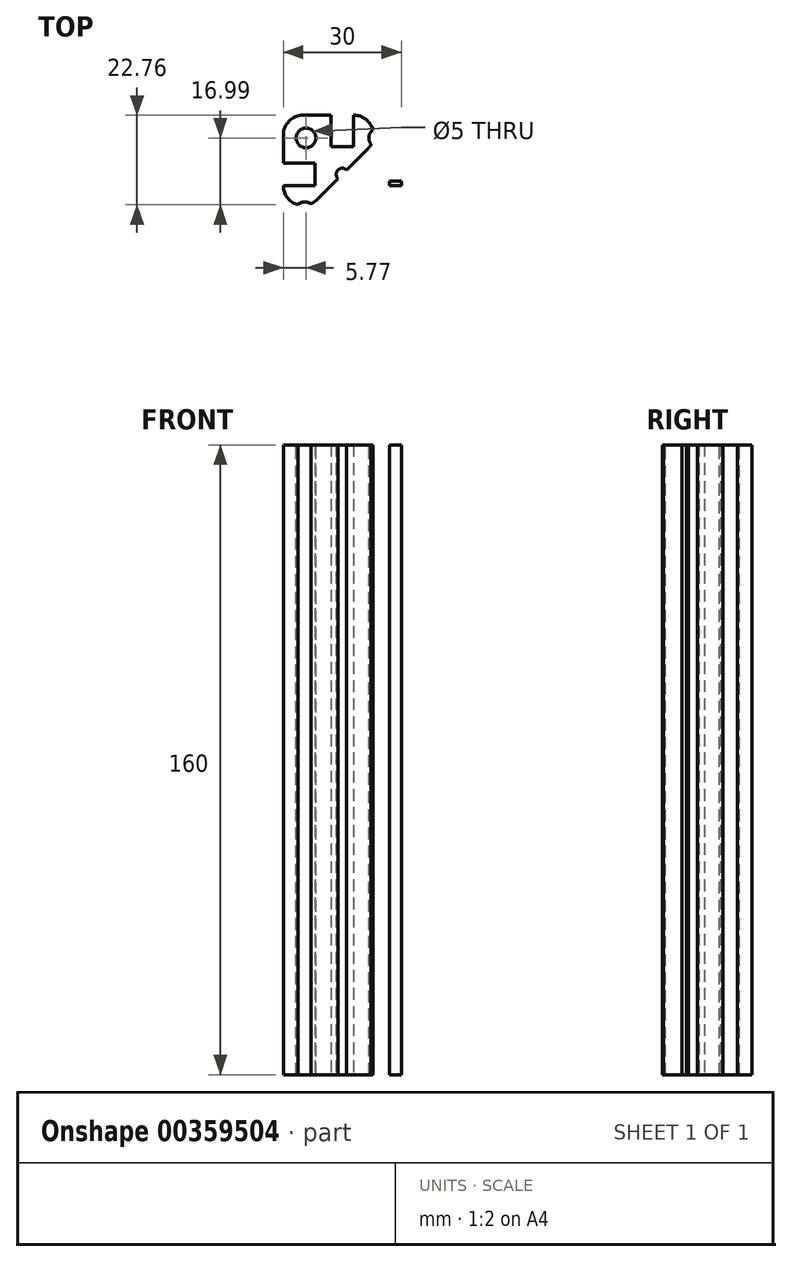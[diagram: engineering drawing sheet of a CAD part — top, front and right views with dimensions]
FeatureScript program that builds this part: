
annotation { "Feature Type Name" : "Feature", "Feature Type Description" : "" }
export const myFeature = defineFeature(function(context is Context, id is Id, definition is map)
    precondition{}
    {
        {
            var Q0;
            Q0=qCreatedBy(makeId("Top.planeOp"),FACE);
            var sketch = newSketch(context, id + "F0", { "sketchPlane" : qUnion([Q0])});
            skLineSegment(sketch, "E0.bottom", {"start": v(15, 15) * mm, "end": v(-15, 15) * mm});
            skLineSegment(sketch, "E0.top", {"start": v(15, -15) * mm, "end": v(-15, -15) * mm});
            skLineSegment(sketch, "E0.left", {"start": v(15, 15) * mm, "end": v(15, -15) * mm});
            skLineSegment(sketch, "E0.right", {"start": v(-15, 15) * mm, "end": v(-15, -15) * mm});
            skPoint(sketch, "E0.middle", {"position": v(0, 0) * mm});
            skLineSegment(sketch, "E1", {"start": v(0, 0) * mm, "end": v(0, 15) * mm});
            skLineSegment(sketch, "E2", {"start": v(0, 15) * mm, "end": v(-2.85, 15) * mm});
            skLineSegment(sketch, "E3", {"start": v(0, 15) * mm, "end": v(2.85, 15) * mm});
            skLineSegment(sketch, "E4", {"start": v(-2.85, 15) * mm, "end": v(-2.85, 12) * mm});
            skLineSegment(sketch, "E5", {"start": v(2.85, 15) * mm, "end": v(2.85, 12) * mm});
            skLineSegment(sketch, "E6", {"start": v(0, 15) * mm, "end": v(-1.7, 15) * mm});
            skLineSegment(sketch, "E7", {"start": v(0, 15) * mm, "end": v(1.7, 15) * mm});
            skLineSegment(sketch, "E8", {"start": v(1.7, 15) * mm, "end": v(1.7, 12) * mm});
            skLineSegment(sketch, "E9", {"start": v(-1.7, 15) * mm, "end": v(-1.7, 12) * mm});
            skLineSegment(sketch, "E10", {"start": v(1.7, 12) * mm, "end": v(-1.7, 12) * mm});
            skLineSegment(sketch, "E11", {"start": v(-1.7, 12) * mm, "end": v(-2.85, 12) * mm});
            skLineSegment(sketch, "E12", {"start": v(-2.85, 12) * mm, "end": v(-2.85, 7) * mm});
            skLineSegment(sketch, "E13", {"start": v(-2.85, 7) * mm, "end": v(2.85, 7) * mm});
            skLineSegment(sketch, "E14", {"start": v(2.85, 7) * mm, "end": v(2.85, 12) * mm});
            skLineSegment(sketch, "E15", {"start": v(1.7, 12) * mm, "end": v(2.85, 12) * mm});
            skLineSegment(sketch, "E16", {"start": v(-15, 0) * mm, "end": v(-15, 2.85) * mm});
            skLineSegment(sketch, "E17", {"start": v(-15, 0) * mm, "end": v(-15, -2.85) * mm});
            skLineSegment(sketch, "E18", {"start": v(-15, -2.85) * mm, "end": v(-12, -2.85) * mm});
            skLineSegment(sketch, "E19", {"start": v(-12, -2.85) * mm, "end": v(-12, 2.85) * mm});
            skLineSegment(sketch, "E20", {"start": v(-12, 2.85) * mm, "end": v(-15, 2.85) * mm});
            skLineSegment(sketch, "E21", {"start": v(-15, 0) * mm, "end": v(-15, 1.7) * mm});
            skLineSegment(sketch, "E22", {"start": v(-15, 1.7) * mm, "end": v(-12, 1.7) * mm});
            skLineSegment(sketch, "E23", {"start": v(-15, 0) * mm, "end": v(-15, -1.7) * mm});
            skLineSegment(sketch, "E24", {"start": v(-15, -1.7) * mm, "end": v(-12, -1.7) * mm});
            skLineSegment(sketch, "E25", {"start": v(-12, -2.85) * mm, "end": v(-7, -2.85) * mm});
            skLineSegment(sketch, "E26", {"start": v(-7, -2.85) * mm, "end": v(-7, 2.85) * mm});
            skLineSegment(sketch, "E27", {"start": v(-7, 2.85) * mm, "end": v(-12, 2.85) * mm});
            skCircle(sketch, "E28", {"center": v(0, 0) * mm, "radius": 1.55 * mm});
            skLineSegment(sketch, "E29", {"start": v(15, -15) * mm, "end": v(0, 0) * mm});
            skLineSegment(sketch, "E30", {"start": v(15, 15) * mm, "end": v(0, 0) * mm});
            skLineSegment(sketch, "E31", {"start": v(-15, 15) * mm, "end": v(0, 0) * mm});
            skLineSegment(sketch, "E32", {"start": v(-15, -15) * mm, "end": v(0, 0) * mm});
            skLineSegment(sketch, "E33", {"start": v(-7.5, -7.5) * mm, "end": v(-15, -15) * mm});
            skLineSegment(sketch, "E34", {"start": v(7.5, -7.5) * mm, "end": v(15, -15) * mm});
            skLineSegment(sketch, "E35", {"start": v(15, 15) * mm, "end": v(7.5, 7.5) * mm});
            skLineSegment(sketch, "E36", {"start": v(-15, 15) * mm, "end": v(-7.5, 7.5) * mm});
            skLineSegment(sketch, "E37", {"start": v(15, 0) * mm, "end": v(15, 2.85) * mm});
            skLineSegment(sketch, "E38", {"start": v(15, 2.85) * mm, "end": v(12, 2.85) * mm});
            skLineSegment(sketch, "E39", {"start": v(12, 2.85) * mm, "end": v(12, -2.85) * mm});
            skLineSegment(sketch, "E40", {"start": v(12, -2.85) * mm, "end": v(15, -2.85) * mm});
            skLineSegment(sketch, "E41", {"start": v(12, -2.85) * mm, "end": v(7, -2.85) * mm});
            skLineSegment(sketch, "E42", {"start": v(7, -2.85) * mm, "end": v(7, 2.85) * mm});
            skLineSegment(sketch, "E43", {"start": v(7, 2.85) * mm, "end": v(12, 2.85) * mm});
            skLineSegment(sketch, "E44", {"start": v(15, 0) * mm, "end": v(15, 1.7) * mm});
            skLineSegment(sketch, "E45", {"start": v(15, 0) * mm, "end": v(15, -1.7) * mm});
            skLineSegment(sketch, "E46", {"start": v(15, -1.7) * mm, "end": v(12, -1.7) * mm});
            skLineSegment(sketch, "E47", {"start": v(15, 1.7) * mm, "end": v(12, 1.7) * mm});
            skLineSegment(sketch, "E48", {"start": v(0, -15) * mm, "end": v(2.85, -15) * mm});
            skLineSegment(sketch, "E49", {"start": v(0, -15) * mm, "end": v(-2.85, -15) * mm});
            skLineSegment(sketch, "E50", {"start": v(-2.85, -15) * mm, "end": v(-2.85, -12) * mm});
            skLineSegment(sketch, "E51", {"start": v(-2.85, -12) * mm, "end": v(2.85, -12) * mm});
            skLineSegment(sketch, "E52", {"start": v(2.85, -12) * mm, "end": v(2.85, -15) * mm});
            skLineSegment(sketch, "E53", {"start": v(2.85, -12) * mm, "end": v(2.85, -7) * mm});
            skLineSegment(sketch, "E54", {"start": v(2.85, -7) * mm, "end": v(-2.85, -7) * mm});
            skLineSegment(sketch, "E55", {"start": v(-2.85, -7) * mm, "end": v(-2.85, -12) * mm});
            skLineSegment(sketch, "E56", {"start": v(0, -15) * mm, "end": v(1.7, -15) * mm});
            skLineSegment(sketch, "E57", {"start": v(1.7, -15) * mm, "end": v(1.7, -12) * mm});
            skLineSegment(sketch, "E58", {"start": v(0, -15) * mm, "end": v(-1.7, -15) * mm});
            skLineSegment(sketch, "E59", {"start": v(-1.7, -15) * mm, "end": v(-1.7, -12) * mm});
            skSolve(sketch);
        }
        {
            var Q0;
            {var subQ5=sQuery(id+"F0.wireOp",EDGE,"E18");Q0=makeQuery(id+"F0.imprint","IMPRINT",FACE,{"disambiguationData":[TD([[makeQuery(id+"F0.imprint","IMPRINT",EDGE,{"derivedFrom":subQ5}),-1.0]])]});}
            var Q1;
            {var subQ1=sQuery(id+"F0.wireOp",EDGE,"E33");Q1=makeQuery(id+"F0.imprint","IMPRINT",FACE,{"disambiguationData":[TD([[makeQuery(id+"F0.imprint","IMPRINT",EDGE,{"derivedFrom":subQ1}),1.0]])]});}
            var Q2;
            {var subQ1=sQuery(id+"F0.wireOp",EDGE,"E4");Q2=makeQuery(id+"F0.imprint","IMPRINT",FACE,{"disambiguationData":[TD([[makeQuery(id+"F0.imprint","IMPRINT",EDGE,{"derivedFrom":subQ1}),-1.0]])]});}
            var Q3;
            {var subQ1=sQuery(id+"F0.wireOp",EDGE,"E34");Q3=makeQuery(id+"F0.imprint","IMPRINT",FACE,{"disambiguationData":[TD([[makeQuery(id+"F0.imprint","IMPRINT",EDGE,{"derivedFrom":subQ1}),1.0]])]});}
            var Q4;
            {var subQ4=sQuery(id+"F0.wireOp",EDGE,"E5");Q4=makeQuery(id+"F0.imprint","IMPRINT",FACE,{"disambiguationData":[TD([[makeQuery(id+"F0.imprint","IMPRINT",EDGE,{"derivedFrom":subQ4}),1.0]])]});}
            var Q5;
            Q5=makeQuery(id+"F0.imprint","IMPRINT",FACE,{"disambiguationData":[TD([[makeQuery(id+"F0.imprint","IMPRINT",EDGE,{"derivedFrom":sQuery(id+"F0.wireOp",EDGE,"E2")}),1.0]])]});
            var Q6;
            Q6=makeQuery(id+"F0.imprint","IMPRINT",FACE,{"disambiguationData":[TD([[makeQuery(id+"F0.imprint","IMPRINT",EDGE,{"derivedFrom":sQuery(id+"F0.wireOp",EDGE,"E3")}),-1.0]])]});
            var Q7;
            Q7=makeQuery(id+"F0.imprint","IMPRINT",FACE,{"disambiguationData":[TD([[makeQuery(id+"F0.imprint","IMPRINT",EDGE,{"derivedFrom":sQuery(id+"F0.wireOp",EDGE,"E16")}),-1.0]])]});
            var Q8;
            Q8=makeQuery(id+"F0.imprint","IMPRINT",FACE,{"disambiguationData":[TD([[makeQuery(id+"F0.imprint","IMPRINT",EDGE,{"derivedFrom":sQuery(id+"F0.wireOp",EDGE,"E17")}),1.0]])]});
            var Q9;
            Q9=makeQuery(id+"F0.imprint","IMPRINT",FACE,{"disambiguationData":[TD([[makeQuery(id+"F0.imprint","IMPRINT",EDGE,{"derivedFrom":sQuery(id+"F0.wireOp",EDGE,"E48")}),1.0]])]});
            var Q10;
            Q10=makeQuery(id+"F0.imprint","IMPRINT",FACE,{"disambiguationData":[TD([[makeQuery(id+"F0.imprint","IMPRINT",EDGE,{"derivedFrom":sQuery(id+"F0.wireOp",EDGE,"E49")}),-1.0]])]});
            var Q11;
            {var subQ0=sQuery(id+"F0.wireOp",EDGE,"E40");Q11=makeQuery(id+"F0.imprint","IMPRINT",FACE,{"disambiguationData":[TD([[makeQuery(id+"F0.imprint","IMPRINT",EDGE,{"derivedFrom":subQ0}),1.0]])]});}
            var Q12;
            Q12=makeQuery(id+"F0.imprint","IMPRINT",FACE,{"disambiguationData":[TD([[makeQuery(id+"F0.imprint","IMPRINT",EDGE,{"derivedFrom":sQuery(id+"F0.wireOp",EDGE,"E37")}),1.0]])]});
            extrude(context, id + "F1", {"entities" : qUnion([Q0, Q1, Q2, Q3, Q4, Q5, Q6, Q7, Q8, Q9, Q10, Q11, Q12]), "depth" : 160 * mm});
        }
        {
            var Q0;
            Q0=makeQuery(id+"F1.opExtrude","SWEPT_EDGE",EDGE,{"disambiguationData":[OSD([sQuery(id+"F0.wireOp",EDGE,"E0.top"),sQuery(id+"F0.wireOp",EDGE,"E0.left"),sQuery(id+"F0.wireOp",EDGE,"E34")])]});
            var Q1;
            Q1=makeQuery(id+"F1.opExtrude","SWEPT_EDGE",EDGE,{"disambiguationData":[OSD([sQuery(id+"F0.wireOp",EDGE,"E0.top"),sQuery(id+"F0.wireOp",EDGE,"E0.right"),sQuery(id+"F0.wireOp",EDGE,"E33")])]});
            var Q2;
            Q2=makeQuery(id+"F1.opExtrude","SWEPT_EDGE",EDGE,{"disambiguationData":[OSD([sQuery(id+"F0.wireOp",EDGE,"E0.bottom"),sQuery(id+"F0.wireOp",EDGE,"E0.left"),sQuery(id+"F0.wireOp",EDGE,"E35")])]});
            var Q3;
            Q3=makeQuery(id+"F1.opExtrude","SWEPT_EDGE",EDGE,{"disambiguationData":[OSD([sQuery(id+"F0.wireOp",EDGE,"E0.bottom"),sQuery(id+"F0.wireOp",EDGE,"E0.right"),sQuery(id+"F0.wireOp",EDGE,"E36")])]});
            fillet(context, id + "F2", {"entities" : qUnion([Q0, Q1, Q2, Q3]), "radius" : 5 * mm, "tangentPropagation" : true, "allowEdgeOverflow" : false});
        }
        {
            var Q0;
            Q0=makeQuery(id+"F1.opExtrude","CAP_FACE",FACE,{"disambiguationData":[OSD([sQuery(id+"F0.wireOp",EDGE,"E0.bottom"),sQuery(id+"F0.wireOp",EDGE,"E0.top"),sQuery(id+"F0.wireOp",EDGE,"E0.left"),sQuery(id+"F0.wireOp",EDGE,"E0.right"),sQuery(id+"F0.wireOp",EDGE,"E2"),sQuery(id+"F0.wireOp",EDGE,"E3"),sQuery(id+"F0.wireOp",EDGE,"E8"),sQuery(id+"F0.wireOp",EDGE,"E9"),sQuery(id+"F0.wireOp",EDGE,"E11"),sQuery(id+"F0.wireOp",EDGE,"E12"),sQuery(id+"F0.wireOp",EDGE,"E13"),sQuery(id+"F0.wireOp",EDGE,"E14"),sQuery(id+"F0.wireOp",EDGE,"E15"),sQuery(id+"F0.wireOp",EDGE,"E16"),sQuery(id+"F0.wireOp",EDGE,"E17"),sQuery(id+"F0.wireOp",EDGE,"E19"),sQuery(id+"F0.wireOp",EDGE,"E22"),sQuery(id+"F0.wireOp",EDGE,"E24"),sQuery(id+"F0.wireOp",EDGE,"E25"),sQuery(id+"F0.wireOp",EDGE,"E26"),sQuery(id+"F0.wireOp",EDGE,"E27"),sQuery(id+"F0.wireOp",EDGE,"E28"),sQuery(id+"F0.wireOp",EDGE,"E37"),sQuery(id+"F0.wireOp",EDGE,"E39"),sQuery(id+"F0.wireOp",EDGE,"E41"),sQuery(id+"F0.wireOp",EDGE,"E42"),sQuery(id+"F0.wireOp",EDGE,"E43"),sQuery(id+"F0.wireOp",EDGE,"E46"),sQuery(id+"F0.wireOp",EDGE,"E47"),sQuery(id+"F0.wireOp",EDGE,"E48"),sQuery(id+"F0.wireOp",EDGE,"E49"),sQuery(id+"F0.wireOp",EDGE,"E51"),sQuery(id+"F0.wireOp",EDGE,"E53"),sQuery(id+"F0.wireOp",EDGE,"E54"),sQuery(id+"F0.wireOp",EDGE,"E55"),sQuery(id+"F0.wireOp",EDGE,"E57"),sQuery(id+"F0.wireOp",EDGE,"E59")])],"isStart":false});
            var sketch = newSketch(context, id + "F3", { "sketchPlane" : qUnion([Q0])});
            skLineSegment(sketch, "E60", {"start": v(-7, 2.85) * mm, "end": v(-2.85, 7) * mm});
            skLineSegment(sketch, "E61", {"start": v(2.85, 7) * mm, "end": v(7, 2.85) * mm});
            skLineSegment(sketch, "E62", {"start": v(2.85, -7) * mm, "end": v(7, -2.85) * mm});
            skLineSegment(sketch, "E63", {"start": v(-7, -2.85) * mm, "end": v(-2.85, -7) * mm});
            skLineSegment(sketch, "E64", {"start": v(-2.85, -7) * mm, "end": v(-4.92, -4.93) * mm});
            skLineSegment(sketch, "E65", {"start": v(-4.92, -4.93) * mm, "end": v(-13.54, -13.54) * mm});
            skLineSegment(sketch, "E66", {"start": v(4.92, -4.93) * mm, "end": v(13.54, -13.54) * mm});
            skLineSegment(sketch, "E67", {"start": v(4.93, 4.93) * mm, "end": v(13.54, 13.54) * mm});
            skLineSegment(sketch, "E68", {"start": v(-4.93, 4.93) * mm, "end": v(-13.54, 13.54) * mm});
            skCircle(sketch, "E69", {"center": v(-9.23, 9.23) * mm, "radius": 2.5 * mm});
            skCircle(sketch, "E70", {"center": v(9.23, 9.23) * mm, "radius": 2.5 * mm});
            skCircle(sketch, "E71", {"center": v(-9.5, -9.5) * mm, "radius": 2.5 * mm});
            skPoint(sketch, "E71.centerSnap0", {"position": v(-2.85, -9.5) * mm});
            skCircle(sketch, "E72", {"center": v(9.23, -9.23) * mm, "radius": 2.5 * mm});
            skSolve(sketch);
        }
        {
            var Q0;
            Q0 = qSketchRegion(id + "F3", true);
            extrude(context, id + "F4", {"entities" : qUnion([Q0]), "operationType" : NewBodyOperationType.REMOVE, "oppositeDirection" : true, "depth" : 200 * mm});
        }
    });
